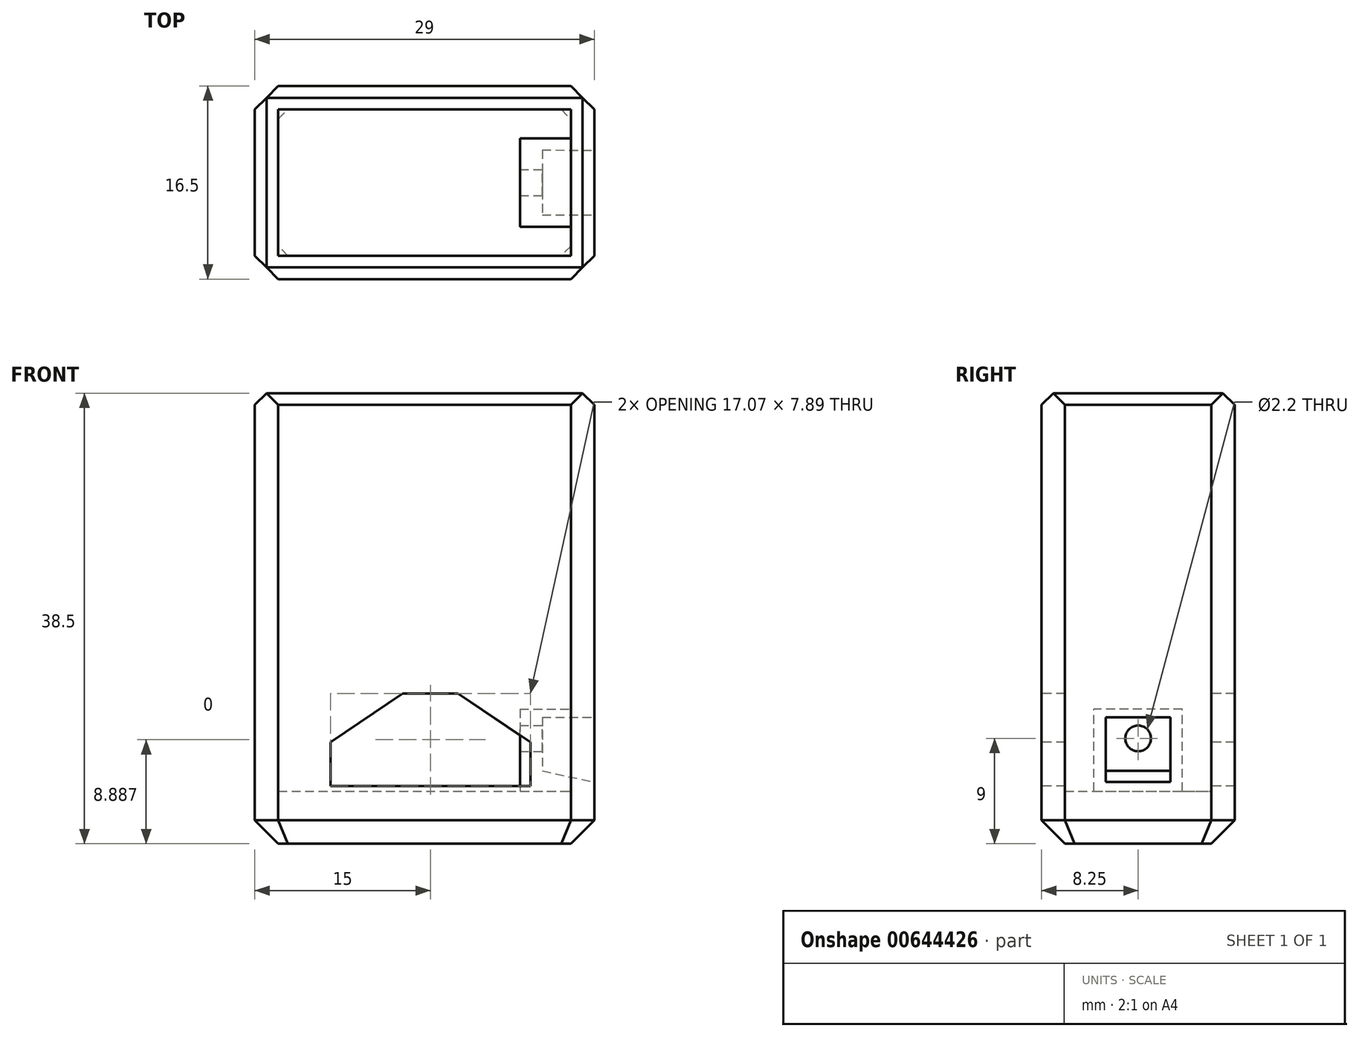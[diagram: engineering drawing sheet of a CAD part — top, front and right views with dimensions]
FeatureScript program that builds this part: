
annotation { "Feature Type Name" : "Feature", "Feature Type Description" : "" }
export const myFeature = defineFeature(function(context is Context, id is Id, definition is map)
    precondition{}
    {
        {
            var Q0;
            Q0=qCreatedBy(makeId("Top.planeOp"),FACE);
            var sketch = newSketch(context, id + "F0", { "sketchPlane" : qUnion([Q0])});
            skLineSegment(sketch, "E0.bottom", {"start": v(0, 0) * mm, "end": v(29, 0) * mm});
            skLineSegment(sketch, "E0.top", {"start": v(0, 16.5) * mm, "end": v(29, 16.5) * mm});
            skLineSegment(sketch, "E0.left", {"start": v(0, 0) * mm, "end": v(0, 16.5) * mm});
            skLineSegment(sketch, "E0.right", {"start": v(29, 0) * mm, "end": v(29, 16.5) * mm});
            skSolve(sketch);
        }
        {
            var Q0;
            Q0=makeQuery(id+"F0.imprint","IMPRINT",FACE,{"disambiguationData":[TD([[makeQuery(id+"F0.imprint","IMPRINT",EDGE,{"derivedFrom":sQuery(id+"F0.wireOp",EDGE,"E0.bottom")}),1.0]])]});
            extrude(context, id + "F1", {"entities" : qUnion([Q0]), "depth" : 38.5 * mm, "offsetDistance" : 25 * mm});
        }
        {
            var Q0;
            Q0=makeQuery(id+"F1.opExtrude","CAP_FACE",FACE,{"disambiguationData":[OSD([sQuery(id+"F0.wireOp",EDGE,"E0.bottom"),sQuery(id+"F0.wireOp",EDGE,"E0.top"),sQuery(id+"F0.wireOp",EDGE,"E0.left"),sQuery(id+"F0.wireOp",EDGE,"E0.right")])],"isStart":false});
            shell(context, id + "F2", {"entities" : qUnion([Q0]), "thickness" : 2 * mm});
        }
        {
            var Q0;
            Q0=makeQuery(id+"F2.opShell","OFFSET_FACE",FACE,{"disambiguationData":[OSD([sQuery(id+"F0.wireOp",EDGE,"E0.bottom"),sQuery(id+"F0.wireOp",EDGE,"E0.top"),sQuery(id+"F0.wireOp",EDGE,"E0.left"),sQuery(id+"F0.wireOp",EDGE,"E0.right")])]});
            extrude(context, id + "F3", {"entities" : qUnion([Q0]), "operationType" : NewBodyOperationType.ADD, "depth" : 2.5 * mm, "offsetDistance" : 25 * mm});
        }
        {
            var Q0;
            Q0=makeQuery(id+"F1.opExtrude","SWEPT_EDGE",EDGE,{"disambiguationData":[OSD([sQuery(id+"F0.wireOp",EDGE,"E0.bottom"),sQuery(id+"F0.wireOp",EDGE,"E0.right")])]});
            var Q1;
            Q1=makeQuery(id+"F1.opExtrude","SWEPT_EDGE",EDGE,{"disambiguationData":[OSD([sQuery(id+"F0.wireOp",EDGE,"E0.top"),sQuery(id+"F0.wireOp",EDGE,"E0.right")])]});
            var Q2;
            Q2=makeQuery(id+"F1.opExtrude","SWEPT_EDGE",EDGE,{"disambiguationData":[OSD([sQuery(id+"F0.wireOp",EDGE,"E0.bottom"),sQuery(id+"F0.wireOp",EDGE,"E0.left")])]});
            var Q3;
            Q3=makeQuery(id+"F1.opExtrude","SWEPT_EDGE",EDGE,{"disambiguationData":[OSD([sQuery(id+"F0.wireOp",EDGE,"E0.top"),sQuery(id+"F0.wireOp",EDGE,"E0.left")])]});
            chamfer(context, id + "F4", {"entities" : qUnion([Q0, Q1, Q2, Q3]), "width" : 2 * mm, "tangentPropagation" : true});
        }
        {
            var Q0;
            Q0=makeQuery(id+"F1.opExtrude","CAP_FACE",FACE,{"disambiguationData":[OSD([sQuery(id+"F0.wireOp",EDGE,"E0.bottom"),sQuery(id+"F0.wireOp",EDGE,"E0.top"),sQuery(id+"F0.wireOp",EDGE,"E0.left"),sQuery(id+"F0.wireOp",EDGE,"E0.right")])],"isStart":true});
            chamfer(context, id + "F5", {"entities" : qUnion([Q0]), "width" : 2 * mm, "tangentPropagation" : true});
        }
        {
            var Q0;
            Q0=makeQuery(id+"F1.opExtrude","CAP_EDGE",EDGE,{"disambiguationData":[OSD([sQuery(id+"F0.wireOp",EDGE,"E0.top")])],"isStart":false});
            var Q1;
            Q1=makeQuery(id+"F1.opExtrude","CAP_EDGE",EDGE,{"disambiguationData":[OSD([sQuery(id+"F0.wireOp",EDGE,"E0.left")])],"isStart":false});
            var Q2;
            Q2=makeQuery(id+"F1.opExtrude","CAP_EDGE",EDGE,{"disambiguationData":[OSD([sQuery(id+"F0.wireOp",EDGE,"E0.bottom")])],"isStart":false});
            var Q3;
            Q3=makeQuery(id+"F1.opExtrude","CAP_EDGE",EDGE,{"disambiguationData":[OSD([sQuery(id+"F0.wireOp",EDGE,"E0.right")])],"isStart":false});
            chamfer(context, id + "F6", {"entities" : qUnion([Q0, Q1, Q2, Q3]), "width" : 1 * mm, "tangentPropagation" : true});
        }
        {
            var Q0;
            Q0=makeQuery(id+"F1.opExtrude","SWEPT_FACE",FACE,{"disambiguationData":[OSD([sQuery(id+"F0.wireOp",EDGE,"E0.bottom")])]});
            var sketch = newSketch(context, id + "F7", { "sketchPlane" : qUnion([Q0])});
            skLineSegment(sketch, "E1", {"start": v(6.46, 8.67) * mm, "end": v(6.46, 4.94) * mm});
            skLineSegment(sketch, "E2", {"start": v(6.46, 4.94) * mm, "end": v(23.54, 4.94) * mm});
            skLineSegment(sketch, "E3", {"start": v(23.54, 4.94) * mm, "end": v(23.54, 8.67) * mm});
            skLineSegment(sketch, "E4", {"start": v(23.54, 8.67) * mm, "end": v(17.36, 12.83) * mm});
            skLineSegment(sketch, "E5", {"start": v(17.36, 12.83) * mm, "end": v(12.63, 12.83) * mm});
            skLineSegment(sketch, "E6", {"start": v(12.64, 12.83) * mm, "end": v(6.46, 8.67) * mm});
            skSolve(sketch);
        }
        {
            var Q0;
            Q0=makeQuery(id+"F7.imprint","IMPRINT",FACE,{"disambiguationData":[TD([[makeQuery(id+"F7.imprint","IMPRINT",EDGE,{"derivedFrom":sQuery(id+"F7.wireOp",EDGE,"E1")}),1.0]])]});
            extrude(context, id + "F8", {"entities" : qUnion([Q0]), "operationType" : NewBodyOperationType.REMOVE, "endBound" : BoundingType.THROUGH_ALL, "oppositeDirection" : true, "depth" : 25 * mm, "offsetDistance" : 25 * mm});
        }
        {
            var Q0;
            Q0=makeQuery(id+"F1.opExtrude","SWEPT_FACE",FACE,{"disambiguationData":[OSD([sQuery(id+"F0.wireOp",EDGE,"E0.right")])]});
            var sketch = newSketch(context, id + "F9", { "sketchPlane" : qUnion([Q0])});
            skLineSegment(sketch, "E7.bottom", {"start": v(4.48, 11.5) * mm, "end": v(12.02, 11.5) * mm});
            skLineSegment(sketch, "E7.top", {"start": v(4.48, 4.25) * mm, "end": v(12.02, 4.25) * mm});
            skLineSegment(sketch, "E7.left", {"start": v(4.48, 11.5) * mm, "end": v(4.48, 4.25) * mm});
            skLineSegment(sketch, "E7.right", {"start": v(12.02, 11.5) * mm, "end": v(12.02, 4.25) * mm});
            skCircle(sketch, "E8", {"center": v(8.25, 9) * mm, "radius": 1.1 * mm});
            skPoint(sketch, "E9", {"position": v(8.25, 11.5) * mm});
            skSolve(sketch);
        }
        {
            var Q0;
            Q0=makeQuery(id+"F9.imprint","IMPRINT",FACE,{"disambiguationData":[TD([[makeQuery(id+"F9.imprint","IMPRINT",EDGE,{"derivedFrom":sQuery(id+"F9.wireOp",EDGE,"E7.bottom")}),-1.0]])]});
            extrude(context, id + "F10", {"entities" : qUnion([Q0]), "operationType" : NewBodyOperationType.ADD, "oppositeDirection" : true, "depth" : 6.35 * mm, "offsetDistance" : 25 * mm});
        }
        {
            var Q0;
            Q0=makeQuery(id+"F1.opExtrude","SWEPT_FACE",FACE,{"disambiguationData":[OSD([sQuery(id+"F0.wireOp",EDGE,"E0.right")])]});
            var sketch = newSketch(context, id + "F11", { "sketchPlane" : qUnion([Q0])});
            skLineSegment(sketch, "E10.bottom", {"start": v(5.48, 10.8) * mm, "end": v(11.01, 10.8) * mm});
            skLineSegment(sketch, "E10.top", {"start": v(5.48, 5.27) * mm, "end": v(11.01, 5.27) * mm});
            skLineSegment(sketch, "E10.left", {"start": v(5.48, 10.8) * mm, "end": v(5.48, 5.27) * mm});
            skLineSegment(sketch, "E10.right", {"start": v(11.01, 10.8) * mm, "end": v(11.01, 5.27) * mm});
            skSolve(sketch);
        }
        {
            var Q0;
            Q0=makeQuery(id+"F11.imprint","IMPRINT",FACE,{"disambiguationData":[TD([[makeQuery(id+"F11.imprint","IMPRINT",EDGE,{"derivedFrom":sQuery(id+"F11.wireOp",EDGE,"E10.bottom")}),1.0]])]});
            cPlane(context, id + "F12", {"entities" : qUnion([Q0]), "cplaneType" : CPlaneType.OFFSET, "offset" : 4.45 * mm, "oppositeDirection" : true, "width" : 150 * mm, "height" : 150 * mm});
        }
        {
            var Q0;
            Q0=qCreatedBy(id+"F12.planeOp",FACE);
            var sketch = newSketch(context, id + "F13", { "sketchPlane" : qUnion([Q0])});
            skLineSegment(sketch, "E11.bottom", {"start": v(11.03, 10.8) * mm, "end": v(5.49, 10.8) * mm});
            skLineSegment(sketch, "E11.top", {"start": v(11.03, 6.22) * mm, "end": v(5.49, 6.22) * mm});
            skLineSegment(sketch, "E11.left", {"start": v(11.03, 10.8) * mm, "end": v(11.03, 6.22) * mm});
            skLineSegment(sketch, "E11.right", {"start": v(5.49, 10.8) * mm, "end": v(5.49, 6.22) * mm});
            skSolve(sketch);
        }
        {
            var Q1;
            Q1 = qSketchRegion(id + "F13", true);
            var Q2;
            Q2 = qSketchRegion(id + "F11", true);
            loft(context, id + "F14", {"operationType" : NewBodyOperationType.REMOVE, "sheetProfilesArray" : [{ "sheetProfileEntities" : qUnion([Q1]) }, { "sheetProfileEntities" : qUnion([Q2]) }]});
        }
    });
